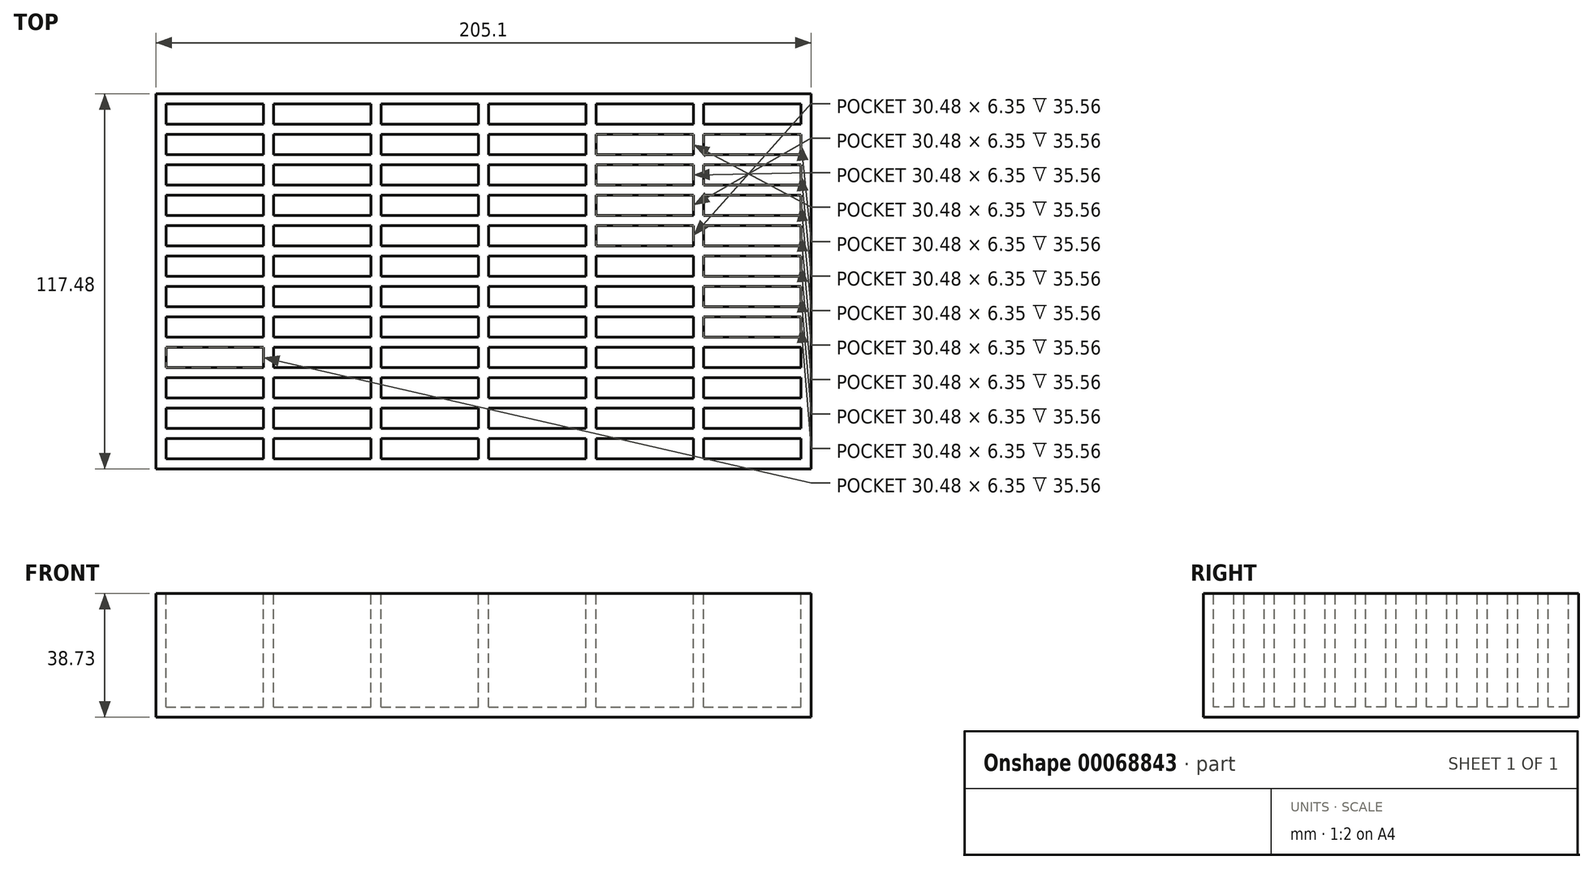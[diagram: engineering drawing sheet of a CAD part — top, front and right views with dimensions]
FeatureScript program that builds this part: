
annotation { "Feature Type Name" : "Feature", "Feature Type Description" : "" }
export const myFeature = defineFeature(function(context is Context, id is Id, definition is map)
    precondition{}
    {
        {
            var Q0;
            Q0=qCreatedBy(makeId("Top.planeOp"),FACE);
            var sketch = newSketch(context, id + "F0", { "sketchPlane" : qUnion([Q0])});
            skLineSegment(sketch, "E0.rect.bottom", {"start": v(102.55, 58.74) * mm, "end": v(-102.55, 58.74) * mm});
            skLineSegment(sketch, "E0.rect.top", {"start": v(102.55, -58.74) * mm, "end": v(-102.55, -58.74) * mm});
            skLineSegment(sketch, "E0.rect.left", {"start": v(102.55, 58.74) * mm, "end": v(102.55, -58.74) * mm});
            skLineSegment(sketch, "E0.rect.right", {"start": v(-102.55, 58.74) * mm, "end": v(-102.55, -58.74) * mm});
            skPoint(sketch, "E0.rect.middle", {"position": v(0, 0) * mm});
            skSolve(sketch);
        }
        {
            var Q0;
            Q0=makeQuery(id+"F0.imprint","IMPRINT",FACE,{"disambiguationData":[TD([[makeQuery(id+"F0.imprint","IMPRINT",EDGE,{"derivedFrom":sQuery(id+"F0.wireOp",EDGE,"E0.rect.bottom")}),1.0]])]});
            extrude(context, id + "F1", {"entities" : qUnion([Q0]), "oppositeDirection" : true, "depth" : 38.73 * mm});
        }
        {
            var Q0;
            Q0=makeQuery(id+"F1.opExtrude","CAP_FACE",FACE,{"disambiguationData":[OSD([sQuery(id+"F0.wireOp",EDGE,"E0.rect.bottom"),sQuery(id+"F0.wireOp",EDGE,"E0.rect.top"),sQuery(id+"F0.wireOp",EDGE,"E0.rect.left"),sQuery(id+"F0.wireOp",EDGE,"E0.rect.right")])],"isStart":true});
            var sketch = newSketch(context, id + "F2", { "sketchPlane" : qUnion([Q0])});
            skLineSegment(sketch, "E1.bottom", {"start": v(-99.38, 55.56) * mm, "end": v(-68.9, 55.56) * mm});
            skLineSegment(sketch, "E1.top", {"start": v(-99.38, 49.21) * mm, "end": v(-68.9, 49.21) * mm});
            skLineSegment(sketch, "E1.left", {"start": v(-99.38, 55.56) * mm, "end": v(-99.38, 49.21) * mm});
            skLineSegment(sketch, "E1.right", {"start": v(-68.9, 55.56) * mm, "end": v(-68.9, 49.21) * mm});
            skLineSegment(sketch, "E2.0.1.0", {"start": v(-99.38, 39.69) * mm, "end": v(-68.9, 39.69) * mm});
            skLineSegment(sketch, "E2.0.1.1", {"start": v(-68.9, 46.04) * mm, "end": v(-68.9, 39.69) * mm});
            skLineSegment(sketch, "E2.0.1.2", {"start": v(-99.38, 46.04) * mm, "end": v(-68.9, 46.04) * mm});
            skLineSegment(sketch, "E2.0.1.3", {"start": v(-99.38, 46.04) * mm, "end": v(-99.38, 39.69) * mm});
            skLineSegment(sketch, "E2.0.2.0", {"start": v(-99.38, 30.16) * mm, "end": v(-68.9, 30.16) * mm});
            skLineSegment(sketch, "E2.0.2.1", {"start": v(-68.9, 36.51) * mm, "end": v(-68.9, 30.16) * mm});
            skLineSegment(sketch, "E2.0.2.2", {"start": v(-99.38, 36.51) * mm, "end": v(-68.9, 36.51) * mm});
            skLineSegment(sketch, "E2.0.2.3", {"start": v(-99.38, 36.51) * mm, "end": v(-99.38, 30.16) * mm});
            skLineSegment(sketch, "E2.0.3.0", {"start": v(-99.38, 20.64) * mm, "end": v(-68.9, 20.64) * mm});
            skLineSegment(sketch, "E2.0.3.1", {"start": v(-68.9, 26.99) * mm, "end": v(-68.9, 20.64) * mm});
            skLineSegment(sketch, "E2.0.3.2", {"start": v(-99.38, 26.99) * mm, "end": v(-68.9, 26.99) * mm});
            skLineSegment(sketch, "E2.0.3.3", {"start": v(-99.38, 26.99) * mm, "end": v(-99.38, 20.64) * mm});
            skLineSegment(sketch, "E2.0.4.0", {"start": v(-99.38, 11.11) * mm, "end": v(-68.9, 11.11) * mm});
            skLineSegment(sketch, "E2.0.4.1", {"start": v(-68.9, 17.46) * mm, "end": v(-68.9, 11.11) * mm});
            skLineSegment(sketch, "E2.0.4.2", {"start": v(-99.38, 17.46) * mm, "end": v(-68.9, 17.46) * mm});
            skLineSegment(sketch, "E2.0.4.3", {"start": v(-99.38, 17.46) * mm, "end": v(-99.38, 11.11) * mm});
            skLineSegment(sketch, "E2.0.5.0", {"start": v(-99.38, 1.59) * mm, "end": v(-68.9, 1.59) * mm});
            skLineSegment(sketch, "E2.0.5.1", {"start": v(-68.9, 7.94) * mm, "end": v(-68.9, 1.59) * mm});
            skLineSegment(sketch, "E2.0.5.2", {"start": v(-99.38, 7.94) * mm, "end": v(-68.9, 7.94) * mm});
            skLineSegment(sketch, "E2.0.5.3", {"start": v(-99.38, 7.94) * mm, "end": v(-99.38, 1.59) * mm});
            skLineSegment(sketch, "E2.0.6.0", {"start": v(-99.38, -7.94) * mm, "end": v(-68.9, -7.94) * mm});
            skLineSegment(sketch, "E2.0.6.1", {"start": v(-68.9, -1.59) * mm, "end": v(-68.9, -7.94) * mm});
            skLineSegment(sketch, "E2.0.6.2", {"start": v(-99.38, -1.59) * mm, "end": v(-68.9, -1.59) * mm});
            skLineSegment(sketch, "E2.0.6.3", {"start": v(-99.38, -1.59) * mm, "end": v(-99.38, -7.94) * mm});
            skLineSegment(sketch, "E2.0.7.0", {"start": v(-99.38, -17.46) * mm, "end": v(-68.9, -17.46) * mm});
            skLineSegment(sketch, "E2.0.7.1", {"start": v(-68.9, -11.11) * mm, "end": v(-68.9, -17.46) * mm});
            skLineSegment(sketch, "E2.0.7.2", {"start": v(-99.38, -11.11) * mm, "end": v(-68.9, -11.11) * mm});
            skLineSegment(sketch, "E2.0.7.3", {"start": v(-99.38, -11.11) * mm, "end": v(-99.38, -17.46) * mm});
            skLineSegment(sketch, "E2.1.0.0", {"start": v(-65.72, 49.21) * mm, "end": v(-35.24, 49.21) * mm});
            skLineSegment(sketch, "E2.1.0.1", {"start": v(-35.24, 55.56) * mm, "end": v(-35.24, 49.21) * mm});
            skLineSegment(sketch, "E2.1.0.2", {"start": v(-65.72, 55.56) * mm, "end": v(-35.24, 55.56) * mm});
            skLineSegment(sketch, "E2.1.0.3", {"start": v(-65.72, 55.56) * mm, "end": v(-65.72, 49.21) * mm});
            skLineSegment(sketch, "E2.1.1.0", {"start": v(-65.72, 39.69) * mm, "end": v(-35.24, 39.69) * mm});
            skLineSegment(sketch, "E2.1.1.1", {"start": v(-35.24, 46.04) * mm, "end": v(-35.24, 39.69) * mm});
            skLineSegment(sketch, "E2.1.1.2", {"start": v(-65.72, 46.04) * mm, "end": v(-35.24, 46.04) * mm});
            skLineSegment(sketch, "E2.1.1.3", {"start": v(-65.72, 46.04) * mm, "end": v(-65.72, 39.69) * mm});
            skLineSegment(sketch, "E2.1.2.0", {"start": v(-65.72, 30.16) * mm, "end": v(-35.24, 30.16) * mm});
            skLineSegment(sketch, "E2.1.2.1", {"start": v(-35.24, 36.51) * mm, "end": v(-35.24, 30.16) * mm});
            skLineSegment(sketch, "E2.1.2.2", {"start": v(-65.72, 36.51) * mm, "end": v(-35.24, 36.51) * mm});
            skLineSegment(sketch, "E2.1.2.3", {"start": v(-65.72, 36.51) * mm, "end": v(-65.72, 30.16) * mm});
            skLineSegment(sketch, "E2.1.3.0", {"start": v(-65.72, 20.64) * mm, "end": v(-35.24, 20.64) * mm});
            skLineSegment(sketch, "E2.1.3.1", {"start": v(-35.24, 26.99) * mm, "end": v(-35.24, 20.64) * mm});
            skLineSegment(sketch, "E2.1.3.2", {"start": v(-65.72, 26.99) * mm, "end": v(-35.24, 26.99) * mm});
            skLineSegment(sketch, "E2.1.3.3", {"start": v(-65.72, 26.99) * mm, "end": v(-65.72, 20.64) * mm});
            skLineSegment(sketch, "E2.1.4.0", {"start": v(-65.72, 11.11) * mm, "end": v(-35.24, 11.11) * mm});
            skLineSegment(sketch, "E2.1.4.1", {"start": v(-35.24, 17.46) * mm, "end": v(-35.24, 11.11) * mm});
            skLineSegment(sketch, "E2.1.4.2", {"start": v(-65.72, 17.46) * mm, "end": v(-35.24, 17.46) * mm});
            skLineSegment(sketch, "E2.1.4.3", {"start": v(-65.72, 17.46) * mm, "end": v(-65.72, 11.11) * mm});
            skLineSegment(sketch, "E2.1.5.0", {"start": v(-65.72, 1.59) * mm, "end": v(-35.24, 1.59) * mm});
            skLineSegment(sketch, "E2.1.5.1", {"start": v(-35.24, 7.94) * mm, "end": v(-35.24, 1.59) * mm});
            skLineSegment(sketch, "E2.1.5.2", {"start": v(-65.72, 7.94) * mm, "end": v(-35.24, 7.94) * mm});
            skLineSegment(sketch, "E2.1.5.3", {"start": v(-65.72, 7.94) * mm, "end": v(-65.72, 1.59) * mm});
            skLineSegment(sketch, "E2.1.6.0", {"start": v(-65.72, -7.94) * mm, "end": v(-35.24, -7.94) * mm});
            skLineSegment(sketch, "E2.1.6.1", {"start": v(-35.24, -1.59) * mm, "end": v(-35.24, -7.94) * mm});
            skLineSegment(sketch, "E2.1.6.2", {"start": v(-65.72, -1.59) * mm, "end": v(-35.24, -1.59) * mm});
            skLineSegment(sketch, "E2.1.6.3", {"start": v(-65.72, -1.59) * mm, "end": v(-65.72, -7.94) * mm});
            skLineSegment(sketch, "E2.1.7.0", {"start": v(-65.72, -17.46) * mm, "end": v(-35.24, -17.46) * mm});
            skLineSegment(sketch, "E2.1.7.1", {"start": v(-35.24, -11.11) * mm, "end": v(-35.24, -17.46) * mm});
            skLineSegment(sketch, "E2.1.7.2", {"start": v(-65.72, -11.11) * mm, "end": v(-35.24, -11.11) * mm});
            skLineSegment(sketch, "E2.1.7.3", {"start": v(-65.72, -11.11) * mm, "end": v(-65.72, -17.46) * mm});
            skLineSegment(sketch, "E2.2.0.0", {"start": v(-32.07, 49.21) * mm, "end": v(-1.59, 49.21) * mm});
            skLineSegment(sketch, "E2.2.0.1", {"start": v(-1.59, 55.56) * mm, "end": v(-1.59, 49.21) * mm});
            skLineSegment(sketch, "E2.2.0.2", {"start": v(-32.07, 55.56) * mm, "end": v(-1.59, 55.56) * mm});
            skLineSegment(sketch, "E2.2.0.3", {"start": v(-32.07, 55.56) * mm, "end": v(-32.07, 49.21) * mm});
            skLineSegment(sketch, "E2.2.1.0", {"start": v(-32.07, 39.69) * mm, "end": v(-1.59, 39.69) * mm});
            skLineSegment(sketch, "E2.2.1.1", {"start": v(-1.59, 46.04) * mm, "end": v(-1.59, 39.69) * mm});
            skLineSegment(sketch, "E2.2.1.2", {"start": v(-32.07, 46.04) * mm, "end": v(-1.59, 46.04) * mm});
            skLineSegment(sketch, "E2.2.1.3", {"start": v(-32.07, 46.04) * mm, "end": v(-32.07, 39.69) * mm});
            skLineSegment(sketch, "E2.2.2.0", {"start": v(-32.07, 30.16) * mm, "end": v(-1.59, 30.16) * mm});
            skLineSegment(sketch, "E2.2.2.1", {"start": v(-1.59, 36.51) * mm, "end": v(-1.59, 30.16) * mm});
            skLineSegment(sketch, "E2.2.2.2", {"start": v(-32.07, 36.51) * mm, "end": v(-1.59, 36.51) * mm});
            skLineSegment(sketch, "E2.2.2.3", {"start": v(-32.07, 36.51) * mm, "end": v(-32.07, 30.16) * mm});
            skLineSegment(sketch, "E2.2.3.0", {"start": v(-32.07, 20.64) * mm, "end": v(-1.59, 20.64) * mm});
            skLineSegment(sketch, "E2.2.3.1", {"start": v(-1.59, 26.99) * mm, "end": v(-1.59, 20.64) * mm});
            skLineSegment(sketch, "E2.2.3.2", {"start": v(-32.07, 26.99) * mm, "end": v(-1.59, 26.99) * mm});
            skLineSegment(sketch, "E2.2.3.3", {"start": v(-32.07, 26.99) * mm, "end": v(-32.07, 20.64) * mm});
            skLineSegment(sketch, "E2.2.4.0", {"start": v(-32.07, 11.11) * mm, "end": v(-1.59, 11.11) * mm});
            skLineSegment(sketch, "E2.2.4.1", {"start": v(-1.59, 17.46) * mm, "end": v(-1.59, 11.11) * mm});
            skLineSegment(sketch, "E2.2.4.2", {"start": v(-32.07, 17.46) * mm, "end": v(-1.59, 17.46) * mm});
            skLineSegment(sketch, "E2.2.4.3", {"start": v(-32.07, 17.46) * mm, "end": v(-32.07, 11.11) * mm});
            skLineSegment(sketch, "E2.2.5.0", {"start": v(-32.07, 1.59) * mm, "end": v(-1.59, 1.59) * mm});
            skLineSegment(sketch, "E2.2.5.1", {"start": v(-1.59, 7.94) * mm, "end": v(-1.59, 1.59) * mm});
            skLineSegment(sketch, "E2.2.5.2", {"start": v(-32.07, 7.94) * mm, "end": v(-1.59, 7.94) * mm});
            skLineSegment(sketch, "E2.2.5.3", {"start": v(-32.07, 7.94) * mm, "end": v(-32.07, 1.59) * mm});
            skLineSegment(sketch, "E2.2.6.0", {"start": v(-32.07, -7.94) * mm, "end": v(-1.59, -7.94) * mm});
            skLineSegment(sketch, "E2.2.6.1", {"start": v(-1.59, -1.59) * mm, "end": v(-1.59, -7.94) * mm});
            skLineSegment(sketch, "E2.2.6.2", {"start": v(-32.07, -1.59) * mm, "end": v(-1.59, -1.59) * mm});
            skLineSegment(sketch, "E2.2.6.3", {"start": v(-32.07, -1.59) * mm, "end": v(-32.07, -7.94) * mm});
            skLineSegment(sketch, "E2.2.7.0", {"start": v(-32.07, -17.46) * mm, "end": v(-1.59, -17.46) * mm});
            skLineSegment(sketch, "E2.2.7.1", {"start": v(-1.59, -11.11) * mm, "end": v(-1.59, -17.46) * mm});
            skLineSegment(sketch, "E2.2.7.2", {"start": v(-32.07, -11.11) * mm, "end": v(-1.59, -11.11) * mm});
            skLineSegment(sketch, "E2.2.7.3", {"start": v(-32.07, -11.11) * mm, "end": v(-32.07, -17.46) * mm});
            skLineSegment(sketch, "E2.3.0.0", {"start": v(1.59, 49.21) * mm, "end": v(32.07, 49.21) * mm});
            skLineSegment(sketch, "E2.3.0.1", {"start": v(32.07, 55.56) * mm, "end": v(32.07, 49.21) * mm});
            skLineSegment(sketch, "E2.3.0.2", {"start": v(1.59, 55.56) * mm, "end": v(32.07, 55.56) * mm});
            skLineSegment(sketch, "E2.3.0.3", {"start": v(1.59, 55.56) * mm, "end": v(1.59, 49.21) * mm});
            skLineSegment(sketch, "E2.3.1.0", {"start": v(1.59, 39.69) * mm, "end": v(32.07, 39.69) * mm});
            skLineSegment(sketch, "E2.3.1.1", {"start": v(32.07, 46.04) * mm, "end": v(32.07, 39.69) * mm});
            skLineSegment(sketch, "E2.3.1.2", {"start": v(1.59, 46.04) * mm, "end": v(32.07, 46.04) * mm});
            skLineSegment(sketch, "E2.3.1.3", {"start": v(1.59, 46.04) * mm, "end": v(1.59, 39.69) * mm});
            skLineSegment(sketch, "E2.3.2.0", {"start": v(1.59, 30.16) * mm, "end": v(32.07, 30.16) * mm});
            skLineSegment(sketch, "E2.3.2.1", {"start": v(32.07, 36.51) * mm, "end": v(32.07, 30.16) * mm});
            skLineSegment(sketch, "E2.3.2.2", {"start": v(1.59, 36.51) * mm, "end": v(32.07, 36.51) * mm});
            skLineSegment(sketch, "E2.3.2.3", {"start": v(1.59, 36.51) * mm, "end": v(1.59, 30.16) * mm});
            skLineSegment(sketch, "E2.3.3.0", {"start": v(1.59, 20.64) * mm, "end": v(32.07, 20.64) * mm});
            skLineSegment(sketch, "E2.3.3.1", {"start": v(32.07, 26.99) * mm, "end": v(32.07, 20.64) * mm});
            skLineSegment(sketch, "E2.3.3.2", {"start": v(1.59, 26.99) * mm, "end": v(32.07, 26.99) * mm});
            skLineSegment(sketch, "E2.3.3.3", {"start": v(1.59, 26.99) * mm, "end": v(1.59, 20.64) * mm});
            skLineSegment(sketch, "E2.3.4.0", {"start": v(1.59, 11.11) * mm, "end": v(32.07, 11.11) * mm});
            skLineSegment(sketch, "E2.3.4.1", {"start": v(32.07, 17.46) * mm, "end": v(32.07, 11.11) * mm});
            skLineSegment(sketch, "E2.3.4.2", {"start": v(1.59, 17.46) * mm, "end": v(32.07, 17.46) * mm});
            skLineSegment(sketch, "E2.3.4.3", {"start": v(1.59, 17.46) * mm, "end": v(1.59, 11.11) * mm});
            skLineSegment(sketch, "E2.3.5.0", {"start": v(1.59, 1.59) * mm, "end": v(32.07, 1.59) * mm});
            skLineSegment(sketch, "E2.3.5.1", {"start": v(32.07, 7.94) * mm, "end": v(32.07, 1.59) * mm});
            skLineSegment(sketch, "E2.3.5.2", {"start": v(1.59, 7.94) * mm, "end": v(32.07, 7.94) * mm});
            skLineSegment(sketch, "E2.3.5.3", {"start": v(1.59, 7.94) * mm, "end": v(1.59, 1.59) * mm});
            skLineSegment(sketch, "E2.3.6.0", {"start": v(1.59, -7.94) * mm, "end": v(32.07, -7.94) * mm});
            skLineSegment(sketch, "E2.3.6.1", {"start": v(32.07, -1.59) * mm, "end": v(32.07, -7.94) * mm});
            skLineSegment(sketch, "E2.3.6.2", {"start": v(1.59, -1.59) * mm, "end": v(32.07, -1.59) * mm});
            skLineSegment(sketch, "E2.3.6.3", {"start": v(1.59, -1.59) * mm, "end": v(1.59, -7.94) * mm});
            skLineSegment(sketch, "E2.3.7.0", {"start": v(1.59, -17.46) * mm, "end": v(32.07, -17.46) * mm});
            skLineSegment(sketch, "E2.3.7.1", {"start": v(32.07, -11.11) * mm, "end": v(32.07, -17.46) * mm});
            skLineSegment(sketch, "E2.3.7.2", {"start": v(1.59, -11.11) * mm, "end": v(32.07, -11.11) * mm});
            skLineSegment(sketch, "E2.3.7.3", {"start": v(1.59, -11.11) * mm, "end": v(1.59, -17.46) * mm});
            skLineSegment(sketch, "E2.4.0.0", {"start": v(35.24, 49.21) * mm, "end": v(65.72, 49.21) * mm});
            skLineSegment(sketch, "E2.4.0.1", {"start": v(65.72, 55.56) * mm, "end": v(65.72, 49.21) * mm});
            skLineSegment(sketch, "E2.4.0.2", {"start": v(35.24, 55.56) * mm, "end": v(65.72, 55.56) * mm});
            skLineSegment(sketch, "E2.4.0.3", {"start": v(35.24, 55.56) * mm, "end": v(35.24, 49.21) * mm});
            skLineSegment(sketch, "E2.4.1.0", {"start": v(35.24, 39.69) * mm, "end": v(65.72, 39.69) * mm});
            skLineSegment(sketch, "E2.4.1.1", {"start": v(65.72, 46.04) * mm, "end": v(65.72, 39.69) * mm});
            skLineSegment(sketch, "E2.4.1.2", {"start": v(35.24, 46.04) * mm, "end": v(65.72, 46.04) * mm});
            skLineSegment(sketch, "E2.4.1.3", {"start": v(35.24, 46.04) * mm, "end": v(35.24, 39.69) * mm});
            skLineSegment(sketch, "E2.4.2.0", {"start": v(35.24, 30.16) * mm, "end": v(65.72, 30.16) * mm});
            skLineSegment(sketch, "E2.4.2.1", {"start": v(65.72, 36.51) * mm, "end": v(65.72, 30.16) * mm});
            skLineSegment(sketch, "E2.4.2.2", {"start": v(35.24, 36.51) * mm, "end": v(65.72, 36.51) * mm});
            skLineSegment(sketch, "E2.4.2.3", {"start": v(35.24, 36.51) * mm, "end": v(35.24, 30.16) * mm});
            skLineSegment(sketch, "E2.4.3.0", {"start": v(35.24, 20.64) * mm, "end": v(65.72, 20.64) * mm});
            skLineSegment(sketch, "E2.4.3.1", {"start": v(65.72, 26.99) * mm, "end": v(65.72, 20.64) * mm});
            skLineSegment(sketch, "E2.4.3.2", {"start": v(35.24, 26.99) * mm, "end": v(65.72, 26.99) * mm});
            skLineSegment(sketch, "E2.4.3.3", {"start": v(35.24, 26.99) * mm, "end": v(35.24, 20.64) * mm});
            skLineSegment(sketch, "E2.4.4.0", {"start": v(35.24, 11.11) * mm, "end": v(65.72, 11.11) * mm});
            skLineSegment(sketch, "E2.4.4.1", {"start": v(65.72, 17.46) * mm, "end": v(65.72, 11.11) * mm});
            skLineSegment(sketch, "E2.4.4.2", {"start": v(35.24, 17.46) * mm, "end": v(65.72, 17.46) * mm});
            skLineSegment(sketch, "E2.4.4.3", {"start": v(35.24, 17.46) * mm, "end": v(35.24, 11.11) * mm});
            skLineSegment(sketch, "E2.4.5.0", {"start": v(35.24, 1.59) * mm, "end": v(65.72, 1.59) * mm});
            skLineSegment(sketch, "E2.4.5.1", {"start": v(65.72, 7.94) * mm, "end": v(65.72, 1.59) * mm});
            skLineSegment(sketch, "E2.4.5.2", {"start": v(35.24, 7.94) * mm, "end": v(65.72, 7.94) * mm});
            skLineSegment(sketch, "E2.4.5.3", {"start": v(35.24, 7.94) * mm, "end": v(35.24, 1.59) * mm});
            skLineSegment(sketch, "E2.4.6.0", {"start": v(35.24, -7.94) * mm, "end": v(65.72, -7.94) * mm});
            skLineSegment(sketch, "E2.4.6.1", {"start": v(65.72, -1.59) * mm, "end": v(65.72, -7.94) * mm});
            skLineSegment(sketch, "E2.4.6.2", {"start": v(35.24, -1.59) * mm, "end": v(65.72, -1.59) * mm});
            skLineSegment(sketch, "E2.4.6.3", {"start": v(35.24, -1.59) * mm, "end": v(35.24, -7.94) * mm});
            skLineSegment(sketch, "E2.4.7.0", {"start": v(35.24, -17.46) * mm, "end": v(65.72, -17.46) * mm});
            skLineSegment(sketch, "E2.4.7.1", {"start": v(65.72, -11.11) * mm, "end": v(65.72, -17.46) * mm});
            skLineSegment(sketch, "E2.4.7.2", {"start": v(35.24, -11.11) * mm, "end": v(65.72, -11.11) * mm});
            skLineSegment(sketch, "E2.4.7.3", {"start": v(35.24, -11.11) * mm, "end": v(35.24, -17.46) * mm});
            skLineSegment(sketch, "E2.5.0.0", {"start": v(68.9, 49.21) * mm, "end": v(99.38, 49.21) * mm});
            skLineSegment(sketch, "E2.5.0.1", {"start": v(99.38, 55.56) * mm, "end": v(99.38, 49.21) * mm});
            skLineSegment(sketch, "E2.5.0.2", {"start": v(68.9, 55.56) * mm, "end": v(99.38, 55.56) * mm});
            skLineSegment(sketch, "E2.5.0.3", {"start": v(68.9, 55.56) * mm, "end": v(68.9, 49.21) * mm});
            skLineSegment(sketch, "E2.5.1.0", {"start": v(68.9, 39.69) * mm, "end": v(99.38, 39.69) * mm});
            skLineSegment(sketch, "E2.5.1.1", {"start": v(99.38, 46.04) * mm, "end": v(99.38, 39.69) * mm});
            skLineSegment(sketch, "E2.5.1.2", {"start": v(68.9, 46.04) * mm, "end": v(99.38, 46.04) * mm});
            skLineSegment(sketch, "E2.5.1.3", {"start": v(68.9, 46.04) * mm, "end": v(68.9, 39.69) * mm});
            skLineSegment(sketch, "E2.5.2.0", {"start": v(68.9, 30.16) * mm, "end": v(99.38, 30.16) * mm});
            skLineSegment(sketch, "E2.5.2.1", {"start": v(99.38, 36.51) * mm, "end": v(99.38, 30.16) * mm});
            skLineSegment(sketch, "E2.5.2.2", {"start": v(68.9, 36.51) * mm, "end": v(99.38, 36.51) * mm});
            skLineSegment(sketch, "E2.5.2.3", {"start": v(68.9, 36.51) * mm, "end": v(68.9, 30.16) * mm});
            skLineSegment(sketch, "E2.5.3.0", {"start": v(68.9, 20.64) * mm, "end": v(99.38, 20.64) * mm});
            skLineSegment(sketch, "E2.5.3.1", {"start": v(99.38, 26.99) * mm, "end": v(99.38, 20.64) * mm});
            skLineSegment(sketch, "E2.5.3.2", {"start": v(68.9, 26.99) * mm, "end": v(99.38, 26.99) * mm});
            skLineSegment(sketch, "E2.5.3.3", {"start": v(68.9, 26.99) * mm, "end": v(68.9, 20.64) * mm});
            skLineSegment(sketch, "E2.5.4.0", {"start": v(68.9, 11.11) * mm, "end": v(99.38, 11.11) * mm});
            skLineSegment(sketch, "E2.5.4.1", {"start": v(99.38, 17.46) * mm, "end": v(99.38, 11.11) * mm});
            skLineSegment(sketch, "E2.5.4.2", {"start": v(68.9, 17.46) * mm, "end": v(99.38, 17.46) * mm});
            skLineSegment(sketch, "E2.5.4.3", {"start": v(68.9, 17.46) * mm, "end": v(68.9, 11.11) * mm});
            skLineSegment(sketch, "E2.5.5.0", {"start": v(68.9, 1.59) * mm, "end": v(99.38, 1.59) * mm});
            skLineSegment(sketch, "E2.5.5.1", {"start": v(99.38, 7.94) * mm, "end": v(99.38, 1.59) * mm});
            skLineSegment(sketch, "E2.5.5.2", {"start": v(68.9, 7.94) * mm, "end": v(99.38, 7.94) * mm});
            skLineSegment(sketch, "E2.5.5.3", {"start": v(68.9, 7.94) * mm, "end": v(68.9, 1.59) * mm});
            skLineSegment(sketch, "E2.5.6.0", {"start": v(68.9, -7.94) * mm, "end": v(99.38, -7.94) * mm});
            skLineSegment(sketch, "E2.5.6.1", {"start": v(99.38, -1.59) * mm, "end": v(99.38, -7.94) * mm});
            skLineSegment(sketch, "E2.5.6.2", {"start": v(68.9, -1.59) * mm, "end": v(99.38, -1.59) * mm});
            skLineSegment(sketch, "E2.5.6.3", {"start": v(68.9, -1.59) * mm, "end": v(68.9, -7.94) * mm});
            skLineSegment(sketch, "E2.5.7.0", {"start": v(68.9, -17.46) * mm, "end": v(99.38, -17.46) * mm});
            skLineSegment(sketch, "E2.5.7.1", {"start": v(99.38, -11.11) * mm, "end": v(99.38, -17.46) * mm});
            skLineSegment(sketch, "E2.5.7.2", {"start": v(68.9, -11.11) * mm, "end": v(99.38, -11.11) * mm});
            skLineSegment(sketch, "E2.5.7.3", {"start": v(68.9, -11.11) * mm, "end": v(68.9, -17.46) * mm});
            skLineSegment(sketch, "E2.direction1", {"start": v(-99.38, 49.21) * mm, "end": v(-65.72, 49.21) * mm, "construction": true});
            skLineSegment(sketch, "E2.direction2", {"start": v(-99.38, 49.21) * mm, "end": v(-99.38, 39.69) * mm, "construction": true});
            skLineSegment(sketch, "E3.0.0.8", {"start": v(-99.38, -26.99) * mm, "end": v(-68.9, -26.99) * mm});
            skLineSegment(sketch, "E3.3.0.8", {"start": v(-68.9, -20.64) * mm, "end": v(-68.9, -26.99) * mm});
            skLineSegment(sketch, "E3.6.0.8", {"start": v(-99.38, -20.64) * mm, "end": v(-68.9, -20.64) * mm});
            skLineSegment(sketch, "E3.9.0.8", {"start": v(-99.38, -20.64) * mm, "end": v(-99.38, -26.99) * mm});
            skLineSegment(sketch, "E3.0.1.8", {"start": v(-65.72, -26.99) * mm, "end": v(-35.24, -26.99) * mm});
            skLineSegment(sketch, "E3.3.1.8", {"start": v(-35.24, -20.64) * mm, "end": v(-35.24, -26.99) * mm});
            skLineSegment(sketch, "E3.6.1.8", {"start": v(-65.72, -20.64) * mm, "end": v(-35.24, -20.64) * mm});
            skLineSegment(sketch, "E3.9.1.8", {"start": v(-65.72, -20.64) * mm, "end": v(-65.72, -26.99) * mm});
            skLineSegment(sketch, "E3.0.2.8", {"start": v(-32.07, -26.99) * mm, "end": v(-1.59, -26.99) * mm});
            skLineSegment(sketch, "E3.3.2.8", {"start": v(-1.59, -20.64) * mm, "end": v(-1.59, -26.99) * mm});
            skLineSegment(sketch, "E3.6.2.8", {"start": v(-32.07, -20.64) * mm, "end": v(-1.59, -20.64) * mm});
            skLineSegment(sketch, "E3.9.2.8", {"start": v(-32.07, -20.64) * mm, "end": v(-32.07, -26.99) * mm});
            skLineSegment(sketch, "E3.0.3.8", {"start": v(1.59, -26.99) * mm, "end": v(32.07, -26.99) * mm});
            skLineSegment(sketch, "E3.3.3.8", {"start": v(32.07, -20.64) * mm, "end": v(32.07, -26.99) * mm});
            skLineSegment(sketch, "E3.6.3.8", {"start": v(1.59, -20.64) * mm, "end": v(32.07, -20.64) * mm});
            skLineSegment(sketch, "E3.9.3.8", {"start": v(1.59, -20.64) * mm, "end": v(1.59, -26.99) * mm});
            skLineSegment(sketch, "E3.0.4.8", {"start": v(35.24, -26.99) * mm, "end": v(65.72, -26.99) * mm});
            skLineSegment(sketch, "E3.3.4.8", {"start": v(65.72, -20.64) * mm, "end": v(65.72, -26.99) * mm});
            skLineSegment(sketch, "E3.6.4.8", {"start": v(35.24, -20.64) * mm, "end": v(65.72, -20.64) * mm});
            skLineSegment(sketch, "E3.9.4.8", {"start": v(35.24, -20.64) * mm, "end": v(35.24, -26.99) * mm});
            skLineSegment(sketch, "E3.0.5.8", {"start": v(68.9, -26.99) * mm, "end": v(99.38, -26.99) * mm});
            skLineSegment(sketch, "E3.3.5.8", {"start": v(99.38, -20.64) * mm, "end": v(99.38, -26.99) * mm});
            skLineSegment(sketch, "E3.6.5.8", {"start": v(68.9, -20.64) * mm, "end": v(99.38, -20.64) * mm});
            skLineSegment(sketch, "E3.9.5.8", {"start": v(68.9, -20.64) * mm, "end": v(68.9, -26.99) * mm});
            skLineSegment(sketch, "E4.0.0.9", {"start": v(-99.38, -36.51) * mm, "end": v(-68.9, -36.51) * mm});
            skLineSegment(sketch, "E4.3.0.9", {"start": v(-68.9, -30.16) * mm, "end": v(-68.9, -36.51) * mm});
            skLineSegment(sketch, "E4.6.0.9", {"start": v(-99.38, -30.16) * mm, "end": v(-68.9, -30.16) * mm});
            skLineSegment(sketch, "E4.9.0.9", {"start": v(-99.38, -30.16) * mm, "end": v(-99.38, -36.51) * mm});
            skLineSegment(sketch, "E4.0.1.9", {"start": v(-65.72, -36.51) * mm, "end": v(-35.24, -36.51) * mm});
            skLineSegment(sketch, "E4.3.1.9", {"start": v(-35.24, -30.16) * mm, "end": v(-35.24, -36.51) * mm});
            skLineSegment(sketch, "E4.6.1.9", {"start": v(-65.72, -30.16) * mm, "end": v(-35.24, -30.16) * mm});
            skLineSegment(sketch, "E4.9.1.9", {"start": v(-65.72, -30.16) * mm, "end": v(-65.72, -36.51) * mm});
            skLineSegment(sketch, "E4.0.2.9", {"start": v(-32.07, -36.51) * mm, "end": v(-1.59, -36.51) * mm});
            skLineSegment(sketch, "E4.3.2.9", {"start": v(-1.59, -30.16) * mm, "end": v(-1.59, -36.51) * mm});
            skLineSegment(sketch, "E4.6.2.9", {"start": v(-32.07, -30.16) * mm, "end": v(-1.59, -30.16) * mm});
            skLineSegment(sketch, "E4.9.2.9", {"start": v(-32.07, -30.16) * mm, "end": v(-32.07, -36.51) * mm});
            skLineSegment(sketch, "E4.0.3.9", {"start": v(1.59, -36.51) * mm, "end": v(32.07, -36.51) * mm});
            skLineSegment(sketch, "E4.3.3.9", {"start": v(32.07, -30.16) * mm, "end": v(32.07, -36.51) * mm});
            skLineSegment(sketch, "E4.6.3.9", {"start": v(1.59, -30.16) * mm, "end": v(32.07, -30.16) * mm});
            skLineSegment(sketch, "E4.9.3.9", {"start": v(1.59, -30.16) * mm, "end": v(1.59, -36.51) * mm});
            skLineSegment(sketch, "E4.0.4.9", {"start": v(35.24, -36.51) * mm, "end": v(65.72, -36.51) * mm});
            skLineSegment(sketch, "E4.3.4.9", {"start": v(65.72, -30.16) * mm, "end": v(65.72, -36.51) * mm});
            skLineSegment(sketch, "E4.6.4.9", {"start": v(35.24, -30.16) * mm, "end": v(65.72, -30.16) * mm});
            skLineSegment(sketch, "E4.9.4.9", {"start": v(35.24, -30.16) * mm, "end": v(35.24, -36.51) * mm});
            skLineSegment(sketch, "E4.0.5.9", {"start": v(68.9, -36.51) * mm, "end": v(99.38, -36.51) * mm});
            skLineSegment(sketch, "E4.3.5.9", {"start": v(99.38, -30.16) * mm, "end": v(99.38, -36.51) * mm});
            skLineSegment(sketch, "E4.6.5.9", {"start": v(68.9, -30.16) * mm, "end": v(99.38, -30.16) * mm});
            skLineSegment(sketch, "E4.9.5.9", {"start": v(68.9, -30.16) * mm, "end": v(68.9, -36.51) * mm});
            skLineSegment(sketch, "E5.0.0.10", {"start": v(-99.38, -46.04) * mm, "end": v(-68.9, -46.04) * mm});
            skLineSegment(sketch, "E5.3.0.10", {"start": v(-68.9, -39.69) * mm, "end": v(-68.9, -46.04) * mm});
            skLineSegment(sketch, "E5.6.0.10", {"start": v(-99.38, -39.69) * mm, "end": v(-68.9, -39.69) * mm});
            skLineSegment(sketch, "E5.9.0.10", {"start": v(-99.38, -39.69) * mm, "end": v(-99.38, -46.04) * mm});
            skLineSegment(sketch, "E5.0.0.11", {"start": v(-99.38, -55.56) * mm, "end": v(-68.9, -55.56) * mm});
            skLineSegment(sketch, "E5.3.0.11", {"start": v(-68.9, -49.21) * mm, "end": v(-68.9, -55.56) * mm});
            skLineSegment(sketch, "E5.6.0.11", {"start": v(-99.38, -49.21) * mm, "end": v(-68.9, -49.21) * mm});
            skLineSegment(sketch, "E5.9.0.11", {"start": v(-99.38, -49.21) * mm, "end": v(-99.38, -55.56) * mm});
            skLineSegment(sketch, "E5.0.1.10", {"start": v(-65.72, -46.04) * mm, "end": v(-35.24, -46.04) * mm});
            skLineSegment(sketch, "E5.3.1.10", {"start": v(-35.24, -39.69) * mm, "end": v(-35.24, -46.04) * mm});
            skLineSegment(sketch, "E5.6.1.10", {"start": v(-65.72, -39.69) * mm, "end": v(-35.24, -39.69) * mm});
            skLineSegment(sketch, "E5.9.1.10", {"start": v(-65.72, -39.69) * mm, "end": v(-65.72, -46.04) * mm});
            skLineSegment(sketch, "E5.0.1.11", {"start": v(-65.72, -55.56) * mm, "end": v(-35.24, -55.56) * mm});
            skLineSegment(sketch, "E5.3.1.11", {"start": v(-35.24, -49.21) * mm, "end": v(-35.24, -55.56) * mm});
            skLineSegment(sketch, "E5.6.1.11", {"start": v(-65.72, -49.21) * mm, "end": v(-35.24, -49.21) * mm});
            skLineSegment(sketch, "E5.9.1.11", {"start": v(-65.72, -49.21) * mm, "end": v(-65.72, -55.56) * mm});
            skLineSegment(sketch, "E5.0.2.10", {"start": v(-32.07, -46.04) * mm, "end": v(-1.59, -46.04) * mm});
            skLineSegment(sketch, "E5.3.2.10", {"start": v(-1.59, -39.69) * mm, "end": v(-1.59, -46.04) * mm});
            skLineSegment(sketch, "E5.6.2.10", {"start": v(-32.07, -39.69) * mm, "end": v(-1.59, -39.69) * mm});
            skLineSegment(sketch, "E5.9.2.10", {"start": v(-32.07, -39.69) * mm, "end": v(-32.07, -46.04) * mm});
            skLineSegment(sketch, "E5.0.2.11", {"start": v(-32.07, -55.56) * mm, "end": v(-1.59, -55.56) * mm});
            skLineSegment(sketch, "E5.3.2.11", {"start": v(-1.59, -49.21) * mm, "end": v(-1.59, -55.56) * mm});
            skLineSegment(sketch, "E5.6.2.11", {"start": v(-32.07, -49.21) * mm, "end": v(-1.59, -49.21) * mm});
            skLineSegment(sketch, "E5.9.2.11", {"start": v(-32.07, -49.21) * mm, "end": v(-32.07, -55.56) * mm});
            skLineSegment(sketch, "E5.0.3.10", {"start": v(1.59, -46.04) * mm, "end": v(32.07, -46.04) * mm});
            skLineSegment(sketch, "E5.3.3.10", {"start": v(32.07, -39.69) * mm, "end": v(32.07, -46.04) * mm});
            skLineSegment(sketch, "E5.6.3.10", {"start": v(1.59, -39.69) * mm, "end": v(32.07, -39.69) * mm});
            skLineSegment(sketch, "E5.9.3.10", {"start": v(1.59, -39.69) * mm, "end": v(1.59, -46.04) * mm});
            skLineSegment(sketch, "E5.0.3.11", {"start": v(1.59, -55.56) * mm, "end": v(32.07, -55.56) * mm});
            skLineSegment(sketch, "E5.3.3.11", {"start": v(32.07, -49.21) * mm, "end": v(32.07, -55.56) * mm});
            skLineSegment(sketch, "E5.6.3.11", {"start": v(1.59, -49.21) * mm, "end": v(32.07, -49.21) * mm});
            skLineSegment(sketch, "E5.9.3.11", {"start": v(1.59, -49.21) * mm, "end": v(1.59, -55.56) * mm});
            skLineSegment(sketch, "E5.0.4.10", {"start": v(35.24, -46.04) * mm, "end": v(65.72, -46.04) * mm});
            skLineSegment(sketch, "E5.3.4.10", {"start": v(65.72, -39.69) * mm, "end": v(65.72, -46.04) * mm});
            skLineSegment(sketch, "E5.6.4.10", {"start": v(35.24, -39.69) * mm, "end": v(65.72, -39.69) * mm});
            skLineSegment(sketch, "E5.9.4.10", {"start": v(35.24, -39.69) * mm, "end": v(35.24, -46.04) * mm});
            skLineSegment(sketch, "E5.0.4.11", {"start": v(35.24, -55.56) * mm, "end": v(65.72, -55.56) * mm});
            skLineSegment(sketch, "E5.3.4.11", {"start": v(65.72, -49.21) * mm, "end": v(65.72, -55.56) * mm});
            skLineSegment(sketch, "E5.6.4.11", {"start": v(35.24, -49.21) * mm, "end": v(65.72, -49.21) * mm});
            skLineSegment(sketch, "E5.9.4.11", {"start": v(35.24, -49.21) * mm, "end": v(35.24, -55.56) * mm});
            skLineSegment(sketch, "E5.0.5.10", {"start": v(68.9, -46.04) * mm, "end": v(99.38, -46.04) * mm});
            skLineSegment(sketch, "E5.3.5.10", {"start": v(99.38, -39.69) * mm, "end": v(99.38, -46.04) * mm});
            skLineSegment(sketch, "E5.6.5.10", {"start": v(68.9, -39.69) * mm, "end": v(99.38, -39.69) * mm});
            skLineSegment(sketch, "E5.9.5.10", {"start": v(68.9, -39.69) * mm, "end": v(68.9, -46.04) * mm});
            skLineSegment(sketch, "E5.0.5.11", {"start": v(68.9, -55.56) * mm, "end": v(99.38, -55.56) * mm});
            skLineSegment(sketch, "E5.3.5.11", {"start": v(99.38, -49.21) * mm, "end": v(99.38, -55.56) * mm});
            skLineSegment(sketch, "E5.6.5.11", {"start": v(68.9, -49.21) * mm, "end": v(99.38, -49.21) * mm});
            skLineSegment(sketch, "E5.9.5.11", {"start": v(68.9, -49.21) * mm, "end": v(68.9, -55.56) * mm});
            skSolve(sketch);
        }
        {
            var Q0;
            Q0 = qSketchRegion(id + "F2", true);
            extrude(context, id + "F3", {"entities" : qUnion([Q0]), "operationType" : NewBodyOperationType.REMOVE, "oppositeDirection" : true, "depth" : 35.56 * mm});
        }
    });
